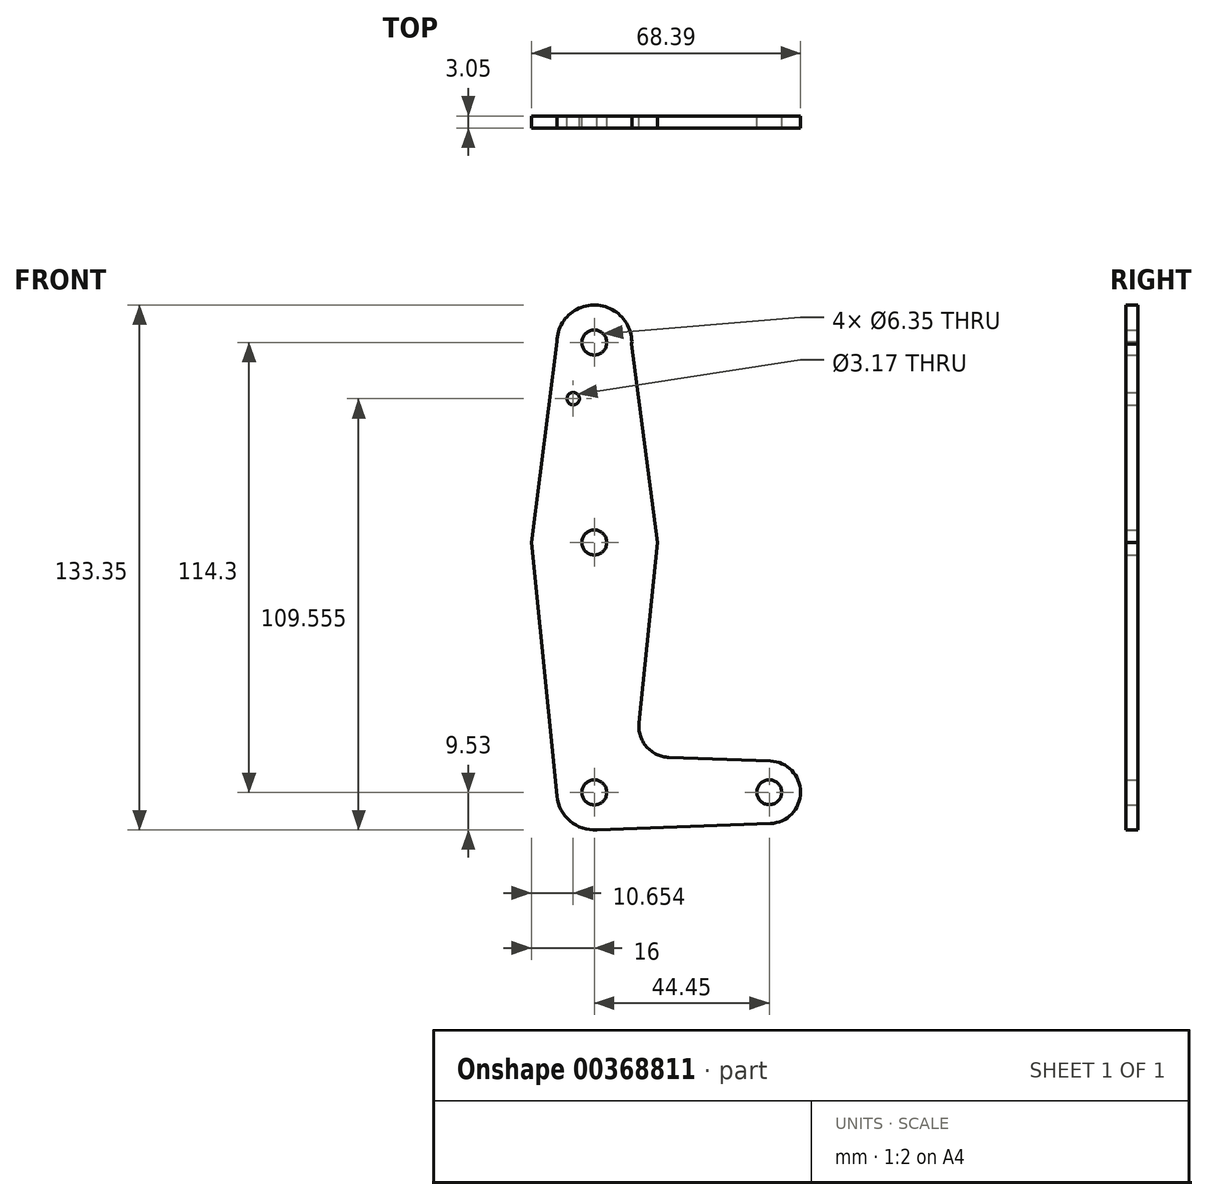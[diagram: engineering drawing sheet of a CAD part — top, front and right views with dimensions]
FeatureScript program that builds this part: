
annotation { "Feature Type Name" : "Feature", "Feature Type Description" : "" }
export const myFeature = defineFeature(function(context is Context, id is Id, definition is map)
    precondition{}
    {
        {
            var Q0;
            Q0=qCreatedBy(makeId("Front.planeOp"),FACE);
            var sketch = newSketch(context, id + "F0", { "sketchPlane" : qUnion([Q0])});
            skCircle(sketch, "E0", {"center": v(0, 0) * mm, "radius": 15.88 * mm});
            skCircle(sketch, "E1", {"center": v(0, 50.8) * mm, "radius": 9.53 * mm});
            skCircle(sketch, "E2", {"center": v(0, -63.5) * mm, "radius": 9.53 * mm});
            skCircle(sketch, "E3", {"center": v(44.45, -63.47) * mm, "radius": 7.94 * mm});
            skLineSegment(sketch, "E4", {"start": v(0, 50.8) * mm, "end": v(0, 0) * mm, "construction": true});
            skLineSegment(sketch, "E5", {"start": v(0, 0) * mm, "end": v(0, -63.5) * mm, "construction": true});
            skLineSegment(sketch, "E6", {"start": v(0, -63.5) * mm, "end": v(44.45, -63.47) * mm, "construction": true});
            skLineSegment(sketch, "E7", {"start": v(-9.52, 51.06) * mm, "end": v(-16, 0) * mm});
            skLineSegment(sketch, "E8", {"start": v(9.51, 50.35) * mm, "end": v(16, 0) * mm});
            skLineSegment(sketch, "E9", {"start": v(-16, 0) * mm, "end": v(-9.48, -64.46) * mm});
            skLineSegment(sketch, "E10", {"start": v(16, 0) * mm, "end": v(11.36, -45.89) * mm});
            skLineSegment(sketch, "E11", {"start": v(19, -54.64) * mm, "end": v(44.73, -55.53) * mm});
            skLineSegment(sketch, "E12", {"start": v(0, -73.03) * mm, "end": v(44.74, -71.4) * mm});
            skCircle(sketch, "E13", {"center": v(0, 50.8) * mm, "radius": 3.18 * mm});
            skCircle(sketch, "E14", {"center": v(0, 0) * mm, "radius": 3.18 * mm});
            skCircle(sketch, "E15", {"center": v(0, -63.5) * mm, "radius": 3.18 * mm});
            skCircle(sketch, "E16", {"center": v(44.45, -63.47) * mm, "radius": 3.18 * mm});
            skCircle(sketch, "E17", {"center": v(-5.35, 36.53) * mm, "radius": 1.59 * mm});
            skPoint(sketch, "E18.newPointA", {"position": v(0, -53.98) * mm});
            skArc(sketch, "E18.filletArc", {"start": v(11.36, -45.89) * mm, "mid": v(13.28, -51.92) * mm, "end": v(19, -54.64) * mm});
            skSolve(sketch);
        }
        {
            var Q0;
            Q0 = qSketchRegion(id + "F0", true);
            extrude(context, id + "F1", {"entities" : qUnion([Q0]), "depth" : 3.05 * mm});
        }
    });
